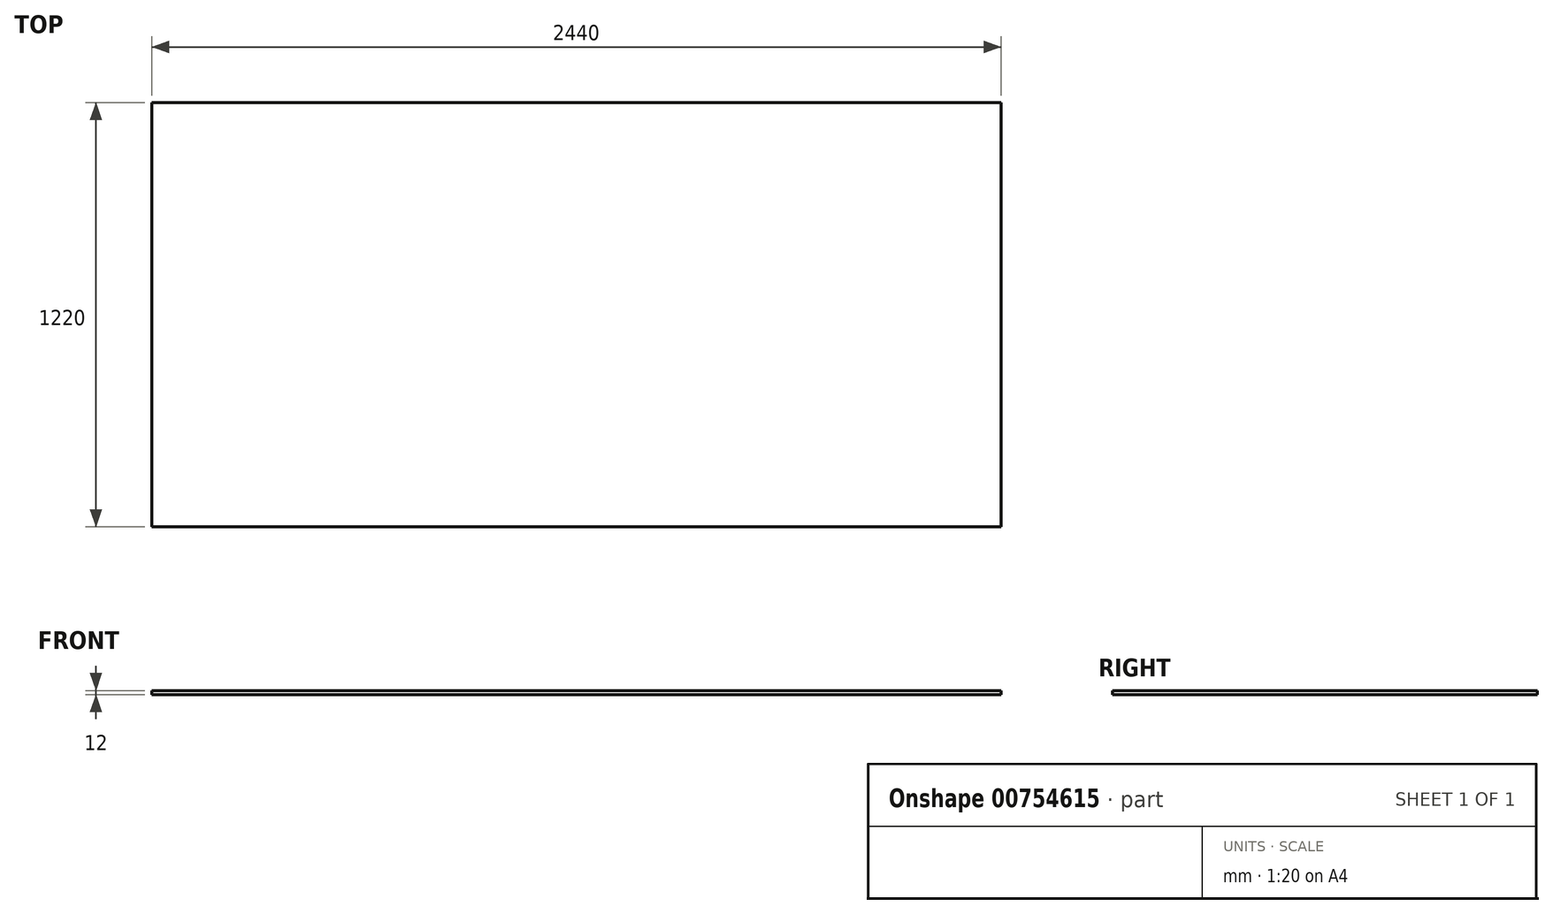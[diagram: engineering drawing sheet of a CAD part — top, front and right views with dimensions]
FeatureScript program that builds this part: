
annotation { "Feature Type Name" : "Feature", "Feature Type Description" : "" }
export const myFeature = defineFeature(function(context is Context, id is Id, definition is map)
    precondition{}
    {
        {
            var Q0;
            Q0=qCreatedBy(makeId("Top.planeOp"),FACE);
            var sketch = newSketch(context, id + "F0", { "sketchPlane" : qUnion([Q0])});
            skLineSegment(sketch, "E0.bottom", {"start": v(1220, 610) * mm, "end": v(-1220, 610) * mm});
            skLineSegment(sketch, "E0.top", {"start": v(1220, -610) * mm, "end": v(-1220, -610) * mm});
            skLineSegment(sketch, "E0.left", {"start": v(1220, 610) * mm, "end": v(1220, -610) * mm});
            skLineSegment(sketch, "E0.right", {"start": v(-1220, 610) * mm, "end": v(-1220, -610) * mm});
            skPoint(sketch, "E0.middle", {"position": v(0, 0) * mm});
            skSolve(sketch);
        }
        {
            var Q0;
            Q0=makeQuery(id+"F0.imprint","IMPRINT",FACE,{"disambiguationData":[TD([[makeQuery(id+"F0.imprint","IMPRINT",EDGE,{"derivedFrom":sQuery(id+"F0.wireOp",EDGE,"E0.bottom")}),1.0]])]});
            extrude(context, id + "F1", {"entities" : qUnion([Q0]), "depth" : 12 * mm, "offsetDistance" : 25 * mm});
        }
    });
